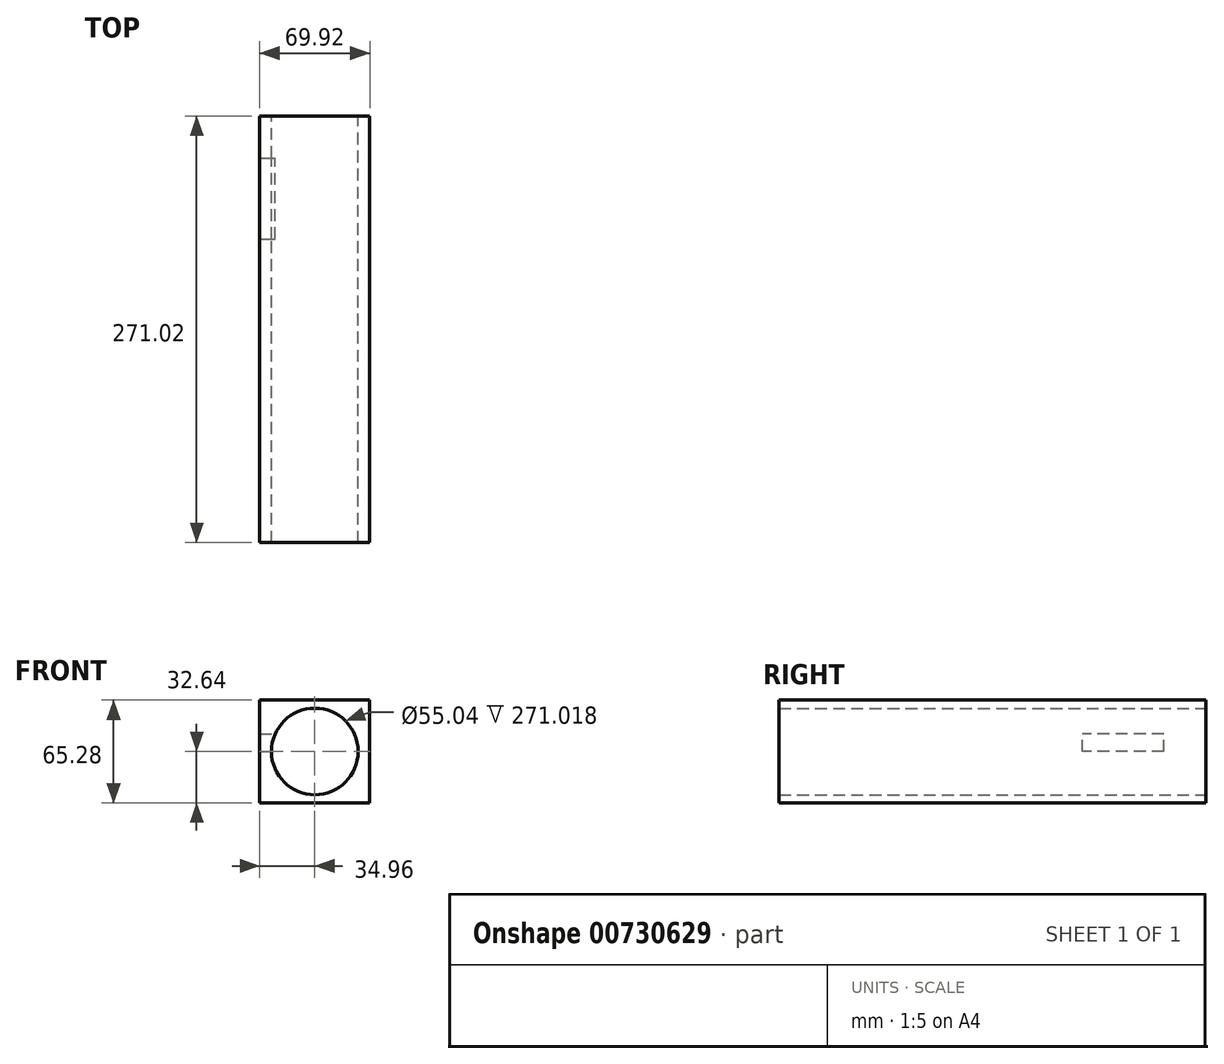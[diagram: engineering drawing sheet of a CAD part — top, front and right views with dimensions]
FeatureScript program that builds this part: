
annotation { "Feature Type Name" : "Feature", "Feature Type Description" : "" }
export const myFeature = defineFeature(function(context is Context, id is Id, definition is map)
    precondition{}
    {
        {
            var Q0;
            Q0=qCreatedBy(makeId("Front.planeOp"),FACE);
            var sketch = newSketch(context, id + "F0", { "sketchPlane" : qUnion([Q0])});
            skLineSegment(sketch, "E0.bottom", {"start": v(-34.96, 32.64) * mm, "end": v(34.96, 32.64) * mm});
            skLineSegment(sketch, "E0.top", {"start": v(-34.96, -32.64) * mm, "end": v(34.96, -32.64) * mm});
            skLineSegment(sketch, "E0.left", {"start": v(-34.96, 32.64) * mm, "end": v(-34.96, -32.64) * mm});
            skLineSegment(sketch, "E0.right", {"start": v(34.96, 32.64) * mm, "end": v(34.96, -32.64) * mm});
            skPoint(sketch, "E0.middle", {"position": v(0, 0) * mm});
            skCircle(sketch, "E1", {"center": v(0, 0) * mm, "radius": 27.52 * mm});
            skSolve(sketch);
        }
        {
            var Q0;
            Q0 = qSketchRegion(id + "F0", true);
            extrude(context, id + "F1", {"entities" : qUnion([Q0]), "depth" : 271.02 * mm, "offsetDistance" : 25.4 * mm});
        }
        {
            var Q0;
            Q0=qCreatedBy(makeId("Right.planeOp"),FACE);
            var sketch = newSketch(context, id + "F2", { "sketchPlane" : qUnion([Q0])});
            skLineSegment(sketch, "E2.bottom", {"start": v(-26.6, 0) * mm, "end": v(-78.17, 0) * mm});
            skLineSegment(sketch, "E2.top", {"start": v(-26.6, 11.04) * mm, "end": v(-78.17, 11.04) * mm});
            skLineSegment(sketch, "E2.left", {"start": v(-26.6, 0) * mm, "end": v(-26.6, 11.04) * mm});
            skLineSegment(sketch, "E2.right", {"start": v(-78.17, 0) * mm, "end": v(-78.17, 11.04) * mm});
            skSolve(sketch);
        }
        {
            var Q0;
            Q0 = qSketchRegion(id + "F2", true);
            extrude(context, id + "F3", {"entities" : qUnion([Q0]), "operationType" : NewBodyOperationType.REMOVE, "oppositeDirection" : true, "depth" : 68.33 * mm, "offsetDistance" : 25.4 * mm});
        }
    });
